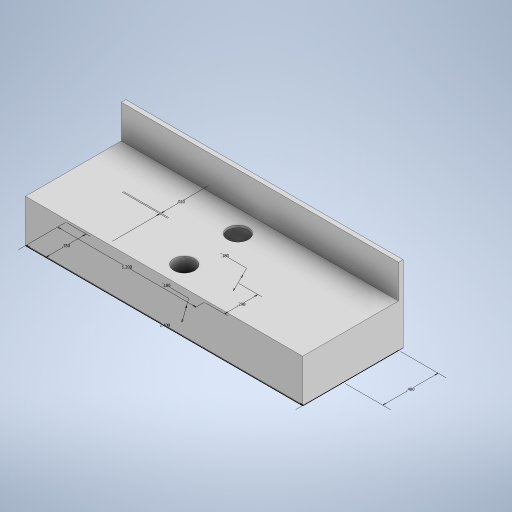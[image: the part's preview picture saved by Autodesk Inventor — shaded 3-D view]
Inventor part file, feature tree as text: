
AUTODESK INVENTOR PART (.ipt)
format: ipt  version: 2024.2 (Build 282272000, 272)  size: 272,384 bytes
history: native  units: in
note: dims shown in document units (in); Inventor stores cm internally (conversion verified against a paired STEP export)
features: extrude x5, sketch x3
ambient origin geometry x8: Origin, YZ Plane, XZ Plane, XY Plane, X Axis, Y Axis, Z Axis, Center Point
bodies: Solid1 (feature_tree)
feature tree (8):
  sketch  "Sketch1"  dims[d0=1.2in d1=2.4in]
  extrude  "Extrusion1"  Depth=2.4in
  extrude  "Extrusion2"  Depth=0.01in
  extrude  "Extrusion3"  Depth=0.175in
  extrude  "Extrusion4"  Depth=0.37in TaperAngle=0.0deg
  extrude  "Extrusion5"  Depth=0.66in TaperAngle=0.0deg
  sketch  "Sketch2"  dims[d2=0.48in d3=0.01in]
  sketch  "Sketch3"  dims[d4=0.29in d5=0.18in d6=0.37in d7=0.0in d8=0.66in d9=0.0in d10=0.29in d11=0.3in d12=0.35in d13=0.0in d14=0.35in d15=0.18in d16=0.37in d17=0.0in d18=0.197in d19=0.197in d20=0.0796in d21=0.0796in d22=0.175in d23=0.0in d24=0.5in d25=0.0344in d26=0.5in d27=0.0344in]
